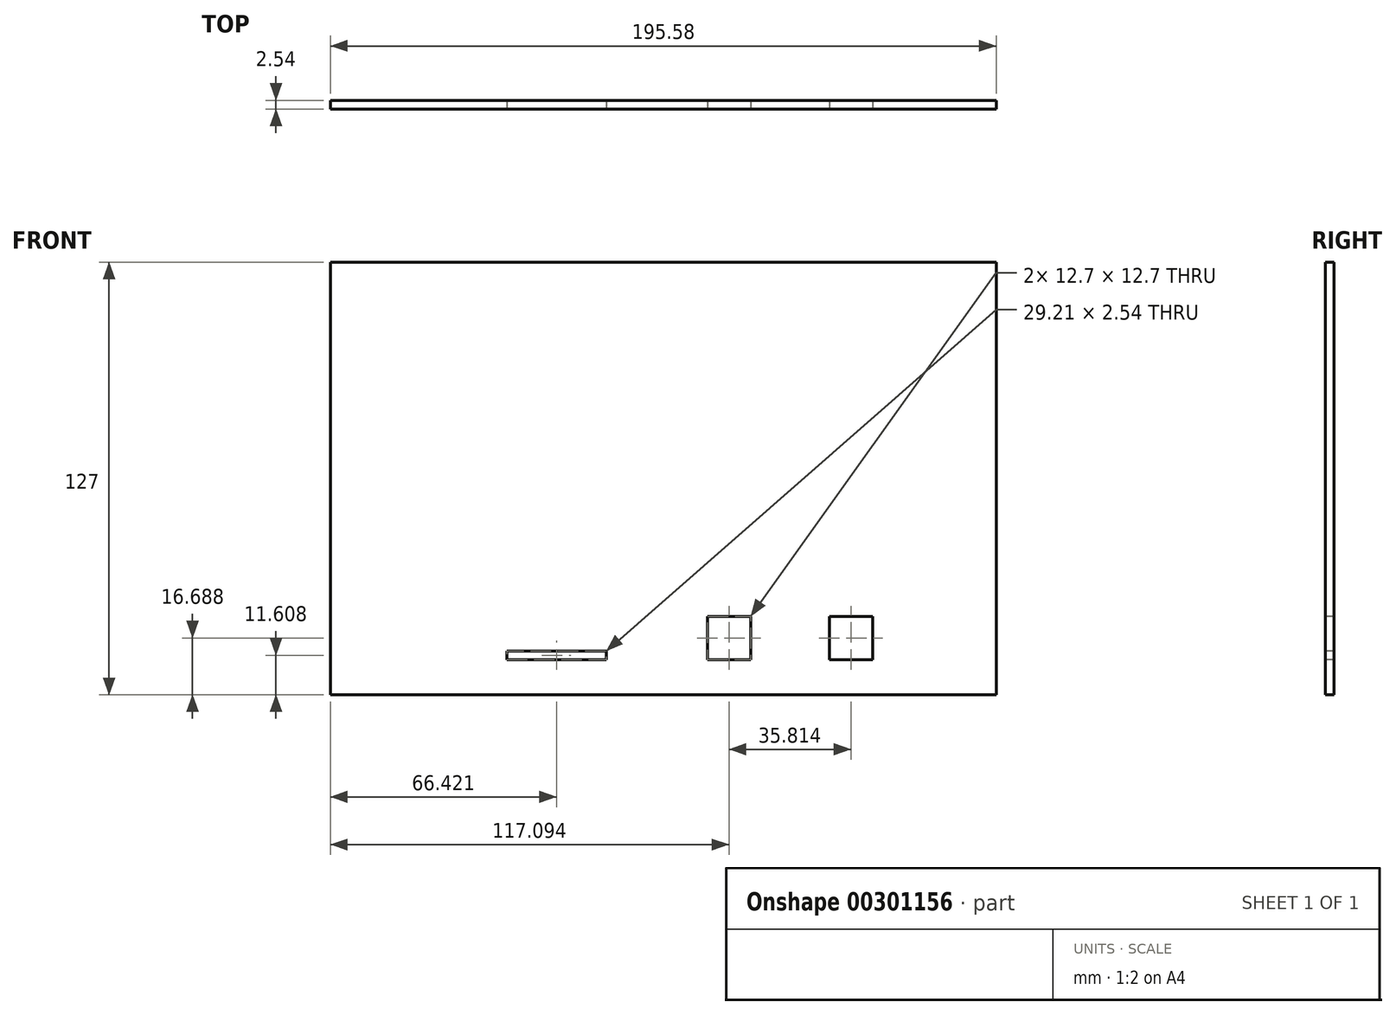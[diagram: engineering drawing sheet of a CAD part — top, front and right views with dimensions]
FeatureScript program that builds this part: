
annotation { "Feature Type Name" : "Feature", "Feature Type Description" : "" }
export const myFeature = defineFeature(function(context is Context, id is Id, definition is map)
    precondition{}
    {
        {
            var Q0;
            Q0=qCreatedBy(makeId("Front.planeOp"),FACE);
            var sketch = newSketch(context, id + "F0", { "sketchPlane" : qUnion([Q0])});
            skLineSegment(sketch, "E0.bottom", {"start": v(97.8, 63.5) * mm, "end": v(-97.8, 63.5) * mm});
            skLineSegment(sketch, "E0.top", {"start": v(97.79, -63.5) * mm, "end": v(-97.79, -63.5) * mm});
            skLineSegment(sketch, "E0.left", {"start": v(97.8, 63.5) * mm, "end": v(97.8, -63.5) * mm});
            skLineSegment(sketch, "E0.right", {"start": v(-97.8, 63.5) * mm, "end": v(-97.8, -63.5) * mm});
            skPoint(sketch, "E0.middle", {"position": v(0, 0) * mm});
            skSolve(sketch);
        }
        {
            var Q0;
            Q0 = qSketchRegion(id + "F0", true);
            extrude(context, id + "F1", {"entities" : qUnion([Q0]), "depth" : 2.54 * mm});
        }
        {
            var Q0;
            Q0=makeQuery(id+"F1.opExtrude","CAP_FACE",FACE,{"disambiguationData":[OSD([sQuery(id+"F0.wireOp",EDGE,"E0.bottom"),sQuery(id+"F0.wireOp",EDGE,"E0.top"),sQuery(id+"F0.wireOp",EDGE,"E0.left"),sQuery(id+"F0.wireOp",EDGE,"E0.right")])],"isStart":false});
            var sketch = newSketch(context, id + "F2", { "sketchPlane" : qUnion([Q0])});
            skLineSegment(sketch, "E1.bottom", {"start": v(-45.97, -50.62) * mm, "end": v(-16.76, -50.62) * mm});
            skLineSegment(sketch, "E1.top", {"start": v(-45.97, -53.16) * mm, "end": v(-16.76, -53.16) * mm});
            skLineSegment(sketch, "E1.left", {"start": v(-45.97, -50.62) * mm, "end": v(-45.97, -53.16) * mm});
            skLineSegment(sketch, "E1.right", {"start": v(-16.76, -50.62) * mm, "end": v(-16.76, -53.16) * mm});
            skLineSegment(sketch, "E2.bottom", {"start": v(12.95, -53.16) * mm, "end": v(25.65, -53.16) * mm});
            skLineSegment(sketch, "E2.top", {"start": v(12.95, -40.46) * mm, "end": v(25.65, -40.46) * mm});
            skLineSegment(sketch, "E2.left", {"start": v(12.95, -53.16) * mm, "end": v(12.95, -40.46) * mm});
            skLineSegment(sketch, "E2.right", {"start": v(25.65, -53.16) * mm, "end": v(25.65, -40.46) * mm});
            skLineSegment(sketch, "E3.bottom", {"start": v(48.77, -53.16) * mm, "end": v(61.47, -53.16) * mm});
            skLineSegment(sketch, "E3.top", {"start": v(48.77, -40.46) * mm, "end": v(61.47, -40.46) * mm});
            skLineSegment(sketch, "E3.left", {"start": v(48.77, -53.16) * mm, "end": v(48.77, -40.46) * mm});
            skLineSegment(sketch, "E3.right", {"start": v(61.47, -53.16) * mm, "end": v(61.47, -40.46) * mm});
            skSolve(sketch);
        }
        {
            var Q0;
            Q0 = qSketchRegion(id + "F2", true);
            extrude(context, id + "F3", {"entities" : qUnion([Q0]), "operationType" : NewBodyOperationType.REMOVE, "oppositeDirection" : true, "depth" : 2.54 * mm});
        }
    });
